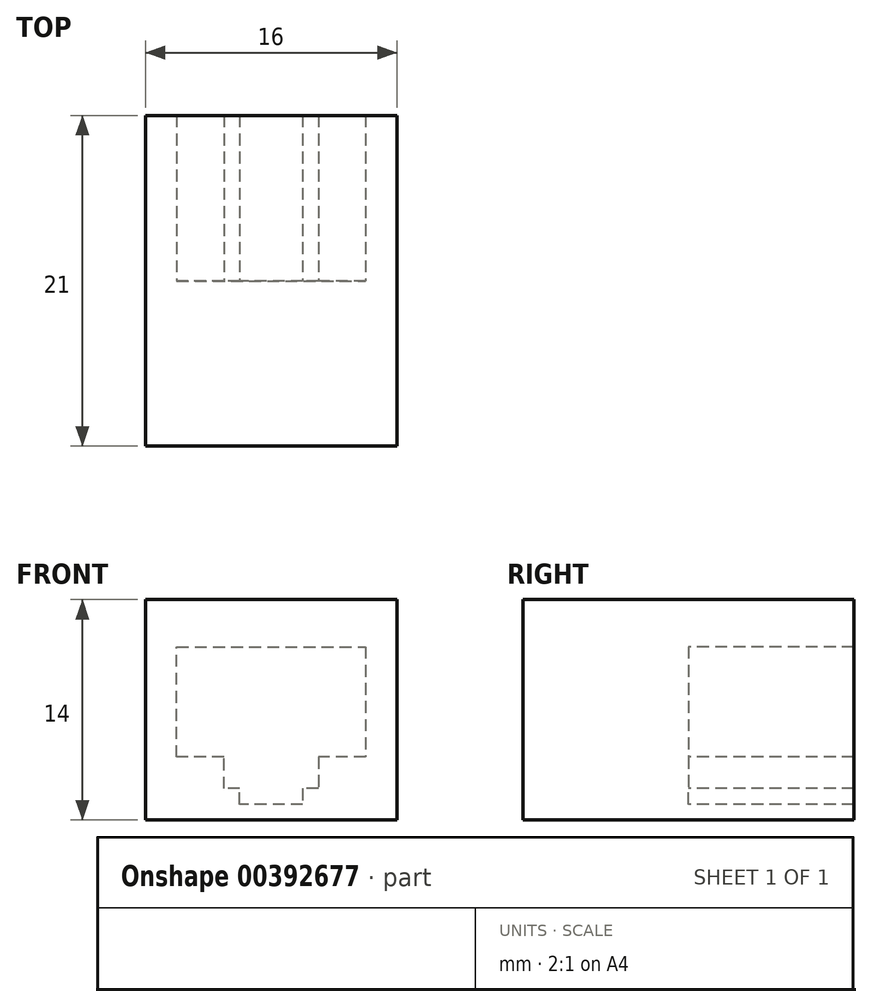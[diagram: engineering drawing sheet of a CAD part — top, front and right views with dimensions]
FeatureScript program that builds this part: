
annotation { "Feature Type Name" : "Feature", "Feature Type Description" : "" }
export const myFeature = defineFeature(function(context is Context, id is Id, definition is map)
    precondition{}
    {
        {
            var Q0;
            Q0=qCreatedBy(makeId("Top.planeOp"),FACE);
            var sketch = newSketch(context, id + "F0", { "sketchPlane" : qUnion([Q0])});
            skLineSegment(sketch, "E0.bottom", {"start": v(8, -10.5) * mm, "end": v(-8, -10.5) * mm});
            skLineSegment(sketch, "E0.top", {"start": v(8, 10.5) * mm, "end": v(-8, 10.5) * mm});
            skLineSegment(sketch, "E0.left", {"start": v(8, -10.5) * mm, "end": v(8, 10.5) * mm});
            skLineSegment(sketch, "E0.right", {"start": v(-8, -10.5) * mm, "end": v(-8, 10.5) * mm});
            skPoint(sketch, "E0.middle", {"position": v(0, 0) * mm});
            skSolve(sketch);
        }
        {
            var Q0;
            Q0 = qSketchRegion(id + "F0", true);
            extrude(context, id + "F1", {"entities" : qUnion([Q0]), "depth" : 14 * mm});
        }
        {
            var Q0;
            Q0=qCreatedBy(makeId("Front.planeOp"),FACE);
            var sketch = newSketch(context, id + "F2", { "sketchPlane" : qUnion([Q0])});
            skLineSegment(sketch, "E1", {"start": v(-2, 1) * mm, "end": v(-2, 2) * mm});
            skLineSegment(sketch, "E2", {"start": v(-2, 2) * mm, "end": v(-3, 2) * mm});
            skLineSegment(sketch, "E3", {"start": v(-3, 2) * mm, "end": v(-3, 4) * mm});
            skLineSegment(sketch, "E4", {"start": v(-3, 4) * mm, "end": v(-6, 4) * mm});
            skLineSegment(sketch, "E5", {"start": v(-6, 4) * mm, "end": v(-6, 11) * mm});
            skLineSegment(sketch, "E6", {"start": v(-6, 11) * mm, "end": v(6, 11) * mm});
            skLineSegment(sketch, "E7", {"start": v(6, 11) * mm, "end": v(6, 4) * mm});
            skLineSegment(sketch, "E8", {"start": v(6, 4) * mm, "end": v(3, 4) * mm});
            skLineSegment(sketch, "E9", {"start": v(3, 4) * mm, "end": v(3, 2) * mm});
            skLineSegment(sketch, "E10", {"start": v(3, 2) * mm, "end": v(2, 2) * mm});
            skLineSegment(sketch, "E11", {"start": v(2, 2) * mm, "end": v(2, 1) * mm});
            skLineSegment(sketch, "E12", {"start": v(2, 1) * mm, "end": v(-2, 1) * mm});
            skLineSegment(sketch, "E13", {"start": v(0, 27.4) * mm, "end": v(0, -6.04) * mm, "construction": true});
            skSolve(sketch);
        }
        {
            var Q0;
            Q0 = qSketchRegion(id + "F2", true);
            extrude(context, id + "F3", {"entities" : qUnion([Q0]), "operationType" : NewBodyOperationType.REMOVE, "oppositeDirection" : true, "depth" : 11 * mm});
        }
    });
